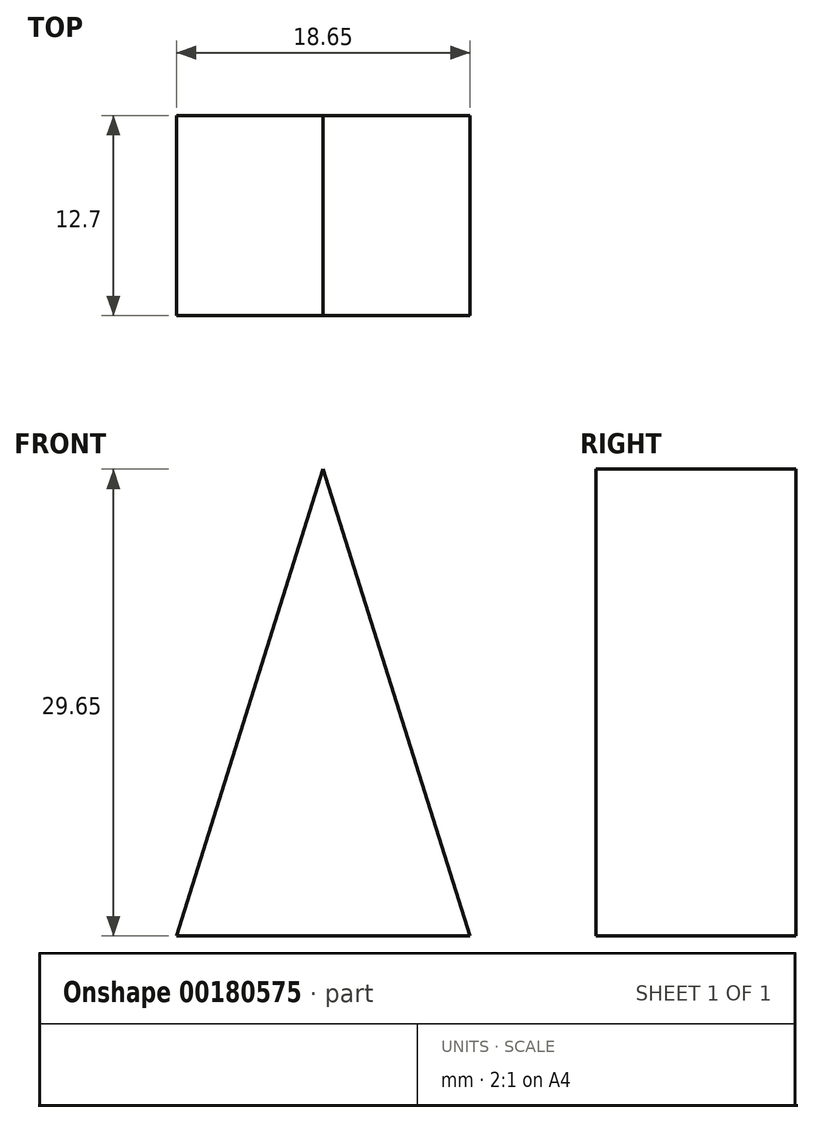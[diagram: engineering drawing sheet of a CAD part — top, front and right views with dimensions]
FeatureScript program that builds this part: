
annotation { "Feature Type Name" : "Feature", "Feature Type Description" : "" }
export const myFeature = defineFeature(function(context is Context, id is Id, definition is map)
    precondition{}
    {
        {
            var Q0;
            Q0=qCreatedBy(makeId("Front.planeOp"),FACE);
            var sketch = newSketch(context, id + "F0", { "sketchPlane" : qUnion([Q0])});
            skLineSegment(sketch, "E0", {"start": v(0, 0) * mm, "end": v(9.33, 29.65) * mm});
            skLineSegment(sketch, "E1", {"start": v(9.33, 29.65) * mm, "end": v(18.65, 0) * mm});
            skLineSegment(sketch, "E2", {"start": v(18.65, 0) * mm, "end": v(0, 0) * mm});
            skSolve(sketch);
        }
        {
            var Q0;
            Q0 = qSketchRegion(id + "F0", true);
            extrude(context, id + "F1", {"entities" : qUnion([Q0]), "depth" : 12.7 * mm});
        }
    });
